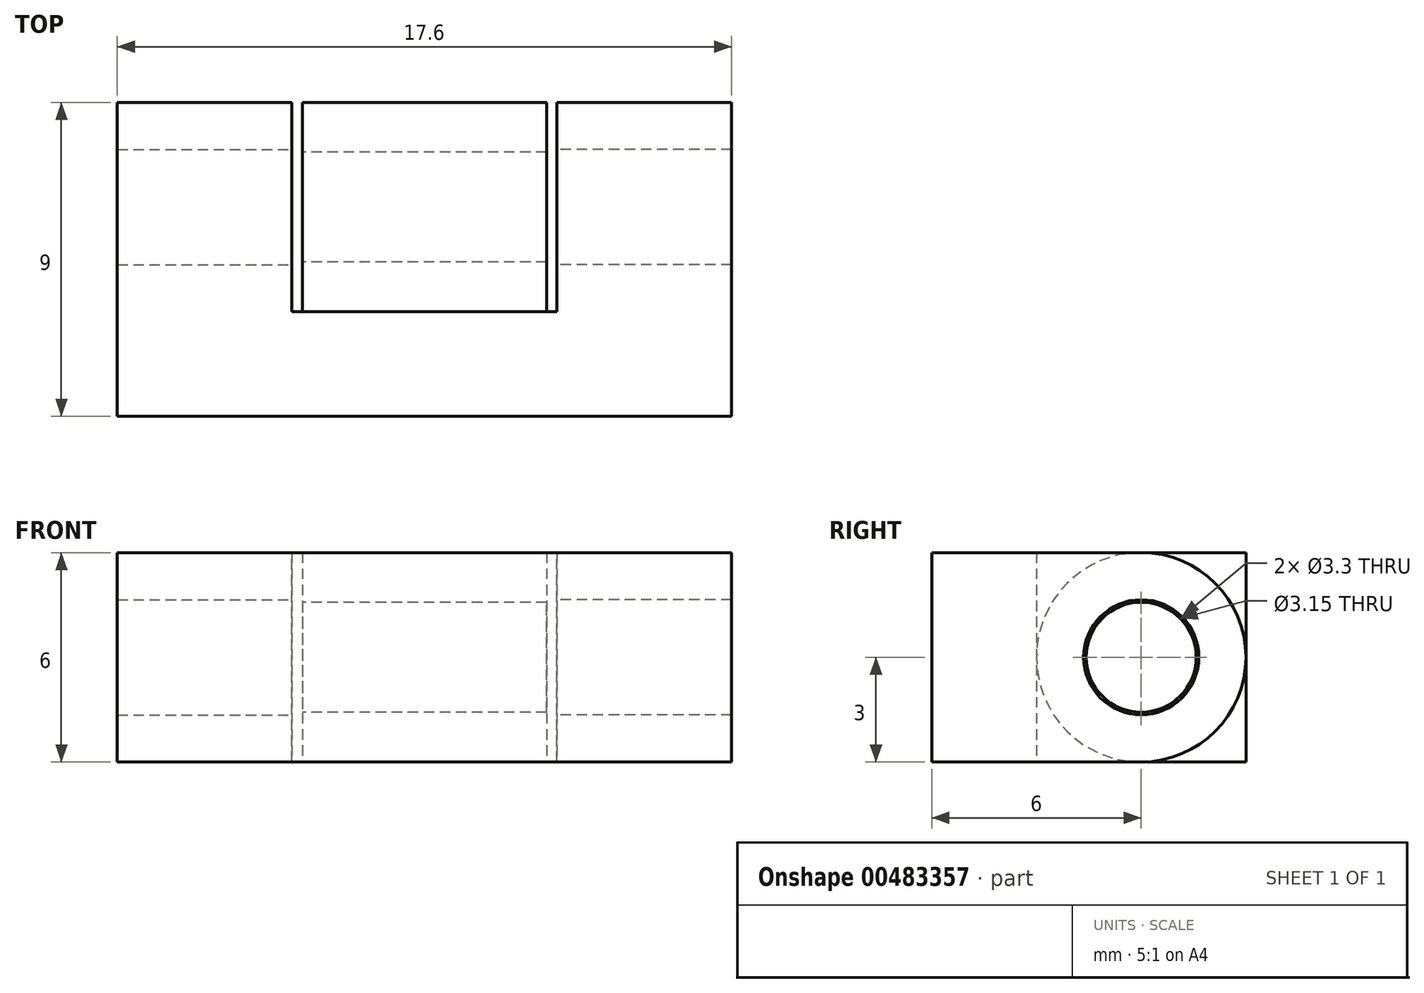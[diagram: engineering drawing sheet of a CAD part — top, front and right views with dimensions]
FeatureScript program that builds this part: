
annotation { "Feature Type Name" : "Feature", "Feature Type Description" : "" }
export const myFeature = defineFeature(function(context is Context, id is Id, definition is map)
    precondition{}
    {
        {
            var Q0;
            Q0=qCreatedBy(makeId("Front.planeOp"),FACE);
            var sketch = newSketch(context, id + "F0", { "sketchPlane" : qUnion([Q0])});
            skLineSegment(sketch, "E0.bottom", {"start": v(3.5, 3) * mm, "end": v(-3.5, 3) * mm});
            skLineSegment(sketch, "E0.top", {"start": v(3.5, -3) * mm, "end": v(-3.5, -3) * mm});
            skLineSegment(sketch, "E0.left", {"start": v(3.5, 3) * mm, "end": v(3.5, -3) * mm});
            skLineSegment(sketch, "E0.right", {"start": v(-3.5, 3) * mm, "end": v(-3.5, -3) * mm});
            skPoint(sketch, "E0.middle", {"position": v(0, 0) * mm});
            skSolve(sketch);
        }
        {
            var Q0;
            Q0=makeQuery(id+"F0.imprint","IMPRINT",FACE,{"disambiguationData":[TD([[makeQuery(id+"F0.imprint","IMPRINT",EDGE,{"derivedFrom":sQuery(id+"F0.wireOp",EDGE,"E0.bottom")}),1.0]])]});
            extrude(context, id + "F1", {"entities" : qUnion([Q0]), "depth" : 6 * mm});
        }
        {
            var Q0;
            Q0=makeQuery(id+"F1.opExtrude","CAP_EDGE",EDGE,{"disambiguationData":[OSD([sQuery(id+"F0.wireOp",EDGE,"E0.bottom")])],"isStart":false});
            var Q1;
            Q1=makeQuery(id+"F1.opExtrude","CAP_EDGE",EDGE,{"disambiguationData":[OSD([sQuery(id+"F0.wireOp",EDGE,"E0.top")])],"isStart":false});
            fillet(context, id + "F2", {"entities" : qUnion([Q0, Q1]), "radius" : 3 * mm, "tangentPropagation" : true, "allowEdgeOverflow" : false});
        }
        {
            var Q0;
            Q0=makeQuery(id+"F1.opExtrude","SWEPT_FACE",FACE,{"disambiguationData":[OSD([sQuery(id+"F0.wireOp",EDGE,"E0.right")])]});
            var sketch = newSketch(context, id + "F3", { "sketchPlane" : qUnion([Q0])});
            skPoint(sketch, "E1", {"position": v(3, 0) * mm});
            skSolve(sketch);
        }
        {
            var Q0;
            Q0=qCreatedBy(makeId("Top.planeOp"),FACE);
            var sketch = newSketch(context, id + "F4", { "sketchPlane" : qUnion([Q0])});
            skLineSegment(sketch, "E2.0", {"start": v(-3.5, -3) * mm, "end": v(-3.5, 0) * mm});
            skLineSegment(sketch, "E3.0", {"start": v(3.5, -3) * mm, "end": v(3.5, 0) * mm});
            skLineSegment(sketch, "E4.0", {"start": v(3.5, 0) * mm, "end": v(-3.5, 0) * mm});
            skLineSegment(sketch, "E5.0", {"start": v(3.5, -3) * mm, "end": v(3.5, -6) * mm});
            skLineSegment(sketch, "E6.0", {"start": v(-3.5, -3) * mm, "end": v(-3.5, -6) * mm});
            skLineSegment(sketch, "E7.0.0", {"start": v(-3.5, -3) * mm, "end": v(3.5, -3) * mm});
            skLineSegment(sketch, "E7.0.2", {"start": v(-3.5, -3) * mm, "end": v(3.5, -3) * mm});
            skLineSegment(sketch, "E8", {"start": v(-3.5, -6) * mm, "end": v(3.5, -6) * mm});
            skLineSegment(sketch, "E9.bottom", {"start": v(-3.8, 0) * mm, "end": v(-8.8, 0) * mm});
            skLineSegment(sketch, "E9.top", {"start": v(-3.8, -6) * mm, "end": v(-8.8, -6) * mm});
            skLineSegment(sketch, "E9.left", {"start": v(-3.8, 0) * mm, "end": v(-3.8, -6) * mm});
            skLineSegment(sketch, "E9.right", {"start": v(-8.8, 0) * mm, "end": v(-8.8, -6) * mm});
            skLineSegment(sketch, "E10.bottom", {"start": v(3.8, 0) * mm, "end": v(8.8, 0) * mm});
            skLineSegment(sketch, "E10.top", {"start": v(3.8, -6) * mm, "end": v(8.8, -6) * mm});
            skLineSegment(sketch, "E10.left", {"start": v(3.8, 0) * mm, "end": v(3.8, -6) * mm});
            skLineSegment(sketch, "E10.right", {"start": v(8.8, 0) * mm, "end": v(8.8, -6) * mm});
            skSolve(sketch);
        }
        {
            var Q0;
            Q0=makeQuery(id+"F4.imprint","IMPRINT",FACE,{"disambiguationData":[TD([[makeQuery(id+"F4.imprint","IMPRINT",EDGE,{"derivedFrom":sQuery(id+"F4.wireOp",EDGE,"E9.bottom")}),1.0]])]});
            var Q1;
            Q1=makeQuery(id+"F4.imprint","IMPRINT",FACE,{"disambiguationData":[TD([[makeQuery(id+"F4.imprint","IMPRINT",EDGE,{"derivedFrom":sQuery(id+"F4.wireOp",EDGE,"E10.bottom")}),-1.0]])]});
            extrude(context, id + "F5", {"entities" : qUnion([Q0, Q1]), "endBound" : BoundingType.SYMMETRIC, "depth" : 6 * mm});
        }
        {
            var Q0;
            Q0=makeQuery(id+"F5.opExtrude","CAP_EDGE",EDGE,{"disambiguationData":[OSD([sQuery(id+"F4.wireOp",EDGE,"E9.bottom")])],"isStart":false});
            var Q1;
            Q1=makeQuery(id+"F5.opExtrude","CAP_EDGE",EDGE,{"disambiguationData":[OSD([sQuery(id+"F4.wireOp",EDGE,"E9.bottom")])],"isStart":true});
            var Q2;
            Q2=makeQuery(id+"F5.opExtrude","CAP_EDGE",EDGE,{"disambiguationData":[OSD([sQuery(id+"F4.wireOp",EDGE,"E10.bottom")])],"isStart":false});
            var Q3;
            Q3=makeQuery(id+"F5.opExtrude","CAP_EDGE",EDGE,{"disambiguationData":[OSD([sQuery(id+"F4.wireOp",EDGE,"E10.bottom")])],"isStart":true});
            fillet(context, id + "F6", {"entities" : qUnion([Q0, Q1, Q2, Q3]), "radius" : 3 * mm, "tangentPropagation" : true, "allowEdgeOverflow" : false});
        }
        {
            var Q0;
            Q0=sQuery(id+"F3.wireOp",VERTEX,"E1");
            var Q1;
            Q1=makeQuery(id+"F1.opExtrude","SWEPT_BODY",BODY,{"disambiguationData":[OSD([sQuery(id+"F0.wireOp",EDGE,"E0.bottom"),sQuery(id+"F0.wireOp",EDGE,"E0.top"),sQuery(id+"F0.wireOp",EDGE,"E0.left"),sQuery(id+"F0.wireOp",EDGE,"E0.right")])]});
            hole(context, id + "F7", {"style" : HoleStyle.SIMPLE, "endStyle" : HoleEndStyle.THROUGH, "standardTappedOrClearance" : lookupTablePath({ "standard" : "ISO", "fit" : "Close", "size" : "M3", "type" : "Clearance" }), "standardBlindInLast" : lookupTablePath({ "fit" : "Close", "standard" : "ISO", "size" : "M3", "type" : "Clearance" }), "holeDiameter" : 3.15 * mm, "isTappedThrough" : true, "tappedDepth" : 12 * mm, "tapClearance" : 3, "locations" : qUnion([Q0]), "scope" : qUnion([Q1])});
        }
        {
            var Q0;
            Q0=sQuery(id+"F3.wireOp",VERTEX,"E1");
            var Q1;
            Q1=makeQuery(id+"F5.opExtrude","SWEPT_BODY",BODY,{"disambiguationData":[OSD([sQuery(id+"F4.wireOp",EDGE,"E10.bottom"),sQuery(id+"F4.wireOp",EDGE,"E10.top"),sQuery(id+"F4.wireOp",EDGE,"E10.left"),sQuery(id+"F4.wireOp",EDGE,"E10.right")])]});
            hole(context, id + "F8", {"style" : HoleStyle.SIMPLE, "endStyle" : HoleEndStyle.THROUGH, "standardTappedOrClearance" : lookupTablePath({ "standard" : "ISO", "fit" : "Normal", "size" : "M3", "type" : "Clearance" }), "standardBlindInLast" : lookupTablePath({ "fit" : "Standard", "standard" : "ISO", "size" : "M3", "type" : "Clearance" }), "holeDiameter" : 3.3 * mm, "isTappedThrough" : true, "tappedDepth" : 12 * mm, "tapClearance" : 3, "locations" : qUnion([Q0]), "scope" : qUnion([Q1])});
        }
        {
            var Q0;
            Q0=sQuery(id+"F3.wireOp",VERTEX,"E1");
            var Q1;
            Q1=makeQuery(id+"F5.opExtrude","SWEPT_BODY",BODY,{"disambiguationData":[OSD([sQuery(id+"F4.wireOp",EDGE,"E9.bottom"),sQuery(id+"F4.wireOp",EDGE,"E9.top"),sQuery(id+"F4.wireOp",EDGE,"E9.left"),sQuery(id+"F4.wireOp",EDGE,"E9.right")])]});
            hole(context, id + "F9", {"style" : HoleStyle.SIMPLE, "endStyle" : HoleEndStyle.THROUGH, "oppositeDirection" : true, "standardTappedOrClearance" : lookupTablePath({ "standard" : "ISO", "fit" : "Normal", "size" : "M3", "type" : "Clearance" }), "standardBlindInLast" : lookupTablePath({ "fit" : "Standard", "standard" : "ISO", "size" : "M3", "type" : "Clearance" }), "holeDiameter" : 3.3 * mm, "isTappedThrough" : true, "tappedDepth" : 12 * mm, "tapClearance" : 3, "locations" : qUnion([Q0]), "scope" : qUnion([Q1])});
        }
        {
            var Q0;
            Q0=makeQuery(id+"F5.opExtrude","SWEPT_FACE",FACE,{"disambiguationData":[OSD([sQuery(id+"F4.wireOp",EDGE,"E9.top")])]});
            var sketch = newSketch(context, id + "F10", { "sketchPlane" : qUnion([Q0])});
            skLineSegment(sketch, "E11.0", {"start": v(8.8, 3) * mm, "end": v(8.8, -3) * mm});
            skLineSegment(sketch, "E12.0", {"start": v(-8.8, 3) * mm, "end": v(-8.8, -3) * mm});
            skLineSegment(sketch, "E13", {"start": v(-8.8, 3) * mm, "end": v(8.8, 3) * mm});
            skLineSegment(sketch, "E14", {"start": v(8.8, -3) * mm, "end": v(-8.8, -3) * mm});
            skSolve(sketch);
        }
        {
            var Q0;
            Q0 = qSketchRegion(id + "F10", true);
            extrude(context, id + "F11", {"entities" : qUnion([Q0]), "operationType" : NewBodyOperationType.ADD, "depth" : 3 * mm});
        }
        {
            var Q0;
            Q0=makeQuery(id+"F1.opExtrude","SWEPT_BODY",BODY,{"disambiguationData":[OSD([sQuery(id+"F0.wireOp",EDGE,"E0.bottom"),sQuery(id+"F0.wireOp",EDGE,"E0.top"),sQuery(id+"F0.wireOp",EDGE,"E0.left"),sQuery(id+"F0.wireOp",EDGE,"E0.right")])]});
            var Q1;
            Q1=makeQuery(id+"F5.opExtrude","SWEPT_BODY",BODY,{"disambiguationData":[OSD([sQuery(id+"F4.wireOp",EDGE,"E9.bottom"),sQuery(id+"F4.wireOp",EDGE,"E9.top"),sQuery(id+"F4.wireOp",EDGE,"E9.left"),sQuery(id+"F4.wireOp",EDGE,"E9.right")])]});
            var Q2;
            Q2=makeQuery(id+"F2.opFillet","BLEND_FACE",FACE,{"disambiguationData":[OSD([sQuery(id+"F0.wireOp",EDGE,"E0.top")])]});
            var Q3;
            Q3=makeQuery(id+"F1.opExtrude","SWEPT_FACE",FACE,{"disambiguationData":[OSD([sQuery(id+"F0.wireOp",EDGE,"E0.left")])]});
            var Q4;
            Q4=makeQuery(id+"F1.opExtrude","SWEPT_FACE",FACE,{"disambiguationData":[OSD([sQuery(id+"F0.wireOp",EDGE,"E0.right")])]});
            booleanBodies(context, id + "F12", {"operationType" : BooleanOperationType.SUBTRACTION, "tools" : qUnion([Q0]), "targets" : qUnion([Q1]), "offset" : true, "entitiesToOffset" : qUnion([Q2, Q3, Q4]), "offsetDistance" : .3 * mm, "keepTools" : true});
        }
    });
